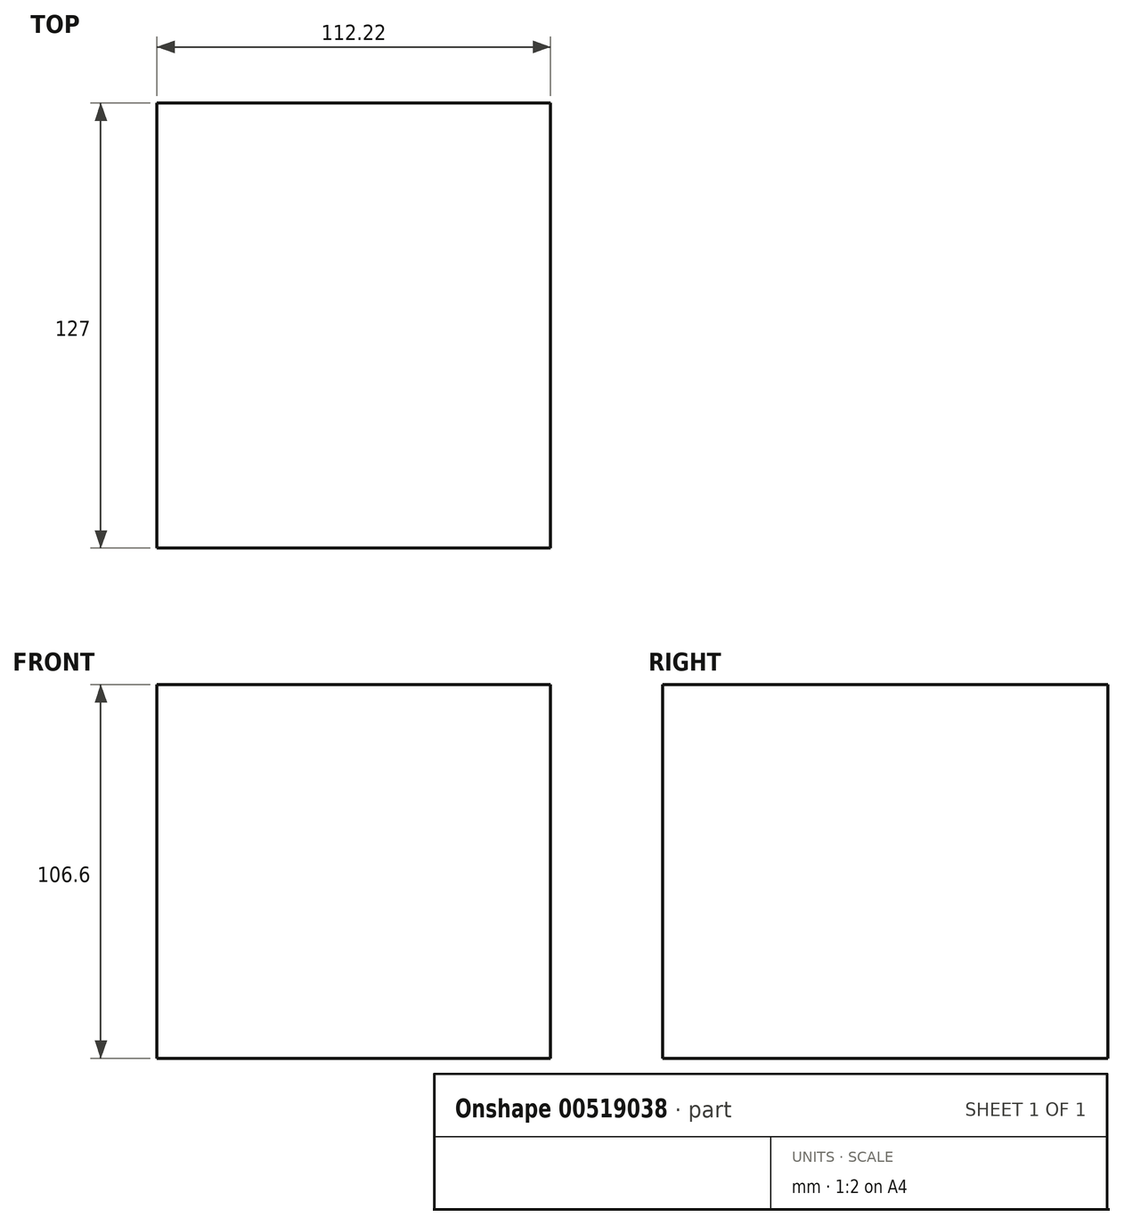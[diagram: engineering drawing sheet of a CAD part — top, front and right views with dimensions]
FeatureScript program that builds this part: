
annotation { "Feature Type Name" : "Feature", "Feature Type Description" : "" }
export const myFeature = defineFeature(function(context is Context, id is Id, definition is map)
    precondition{}
    {
        {
            var Q0;
            Q0=qCreatedBy(makeId("Front.planeOp"),FACE);
            var sketch = newSketch(context, id + "F0", { "sketchPlane" : qUnion([Q0])});
            skLineSegment(sketch, "E0.bottom", {"start": v(-71.04, 51.05) * mm, "end": v(41.18, 51.05) * mm});
            skLineSegment(sketch, "E0.top", {"start": v(-71.04, -55.55) * mm, "end": v(41.18, -55.55) * mm});
            skLineSegment(sketch, "E0.left", {"start": v(-71.04, 51.05) * mm, "end": v(-71.04, -55.55) * mm});
            skLineSegment(sketch, "E0.right", {"start": v(41.18, 51.05) * mm, "end": v(41.18, -55.55) * mm});
            skSolve(sketch);
        }
        {
            var Q0;
            Q0=makeQuery(id+"F0.imprint","IMPRINT",FACE,{"disambiguationData":[TD([[makeQuery(id+"F0.imprint","IMPRINT",EDGE,{"derivedFrom":sQuery(id+"F0.wireOp",EDGE,"E0.bottom")}),-1.0]])]});
            extrude(context, id + "F1", {"entities" : qUnion([Q0]), "depth" : 127 * mm, "offsetDistance" : 25.4 * mm});
        }
    });
